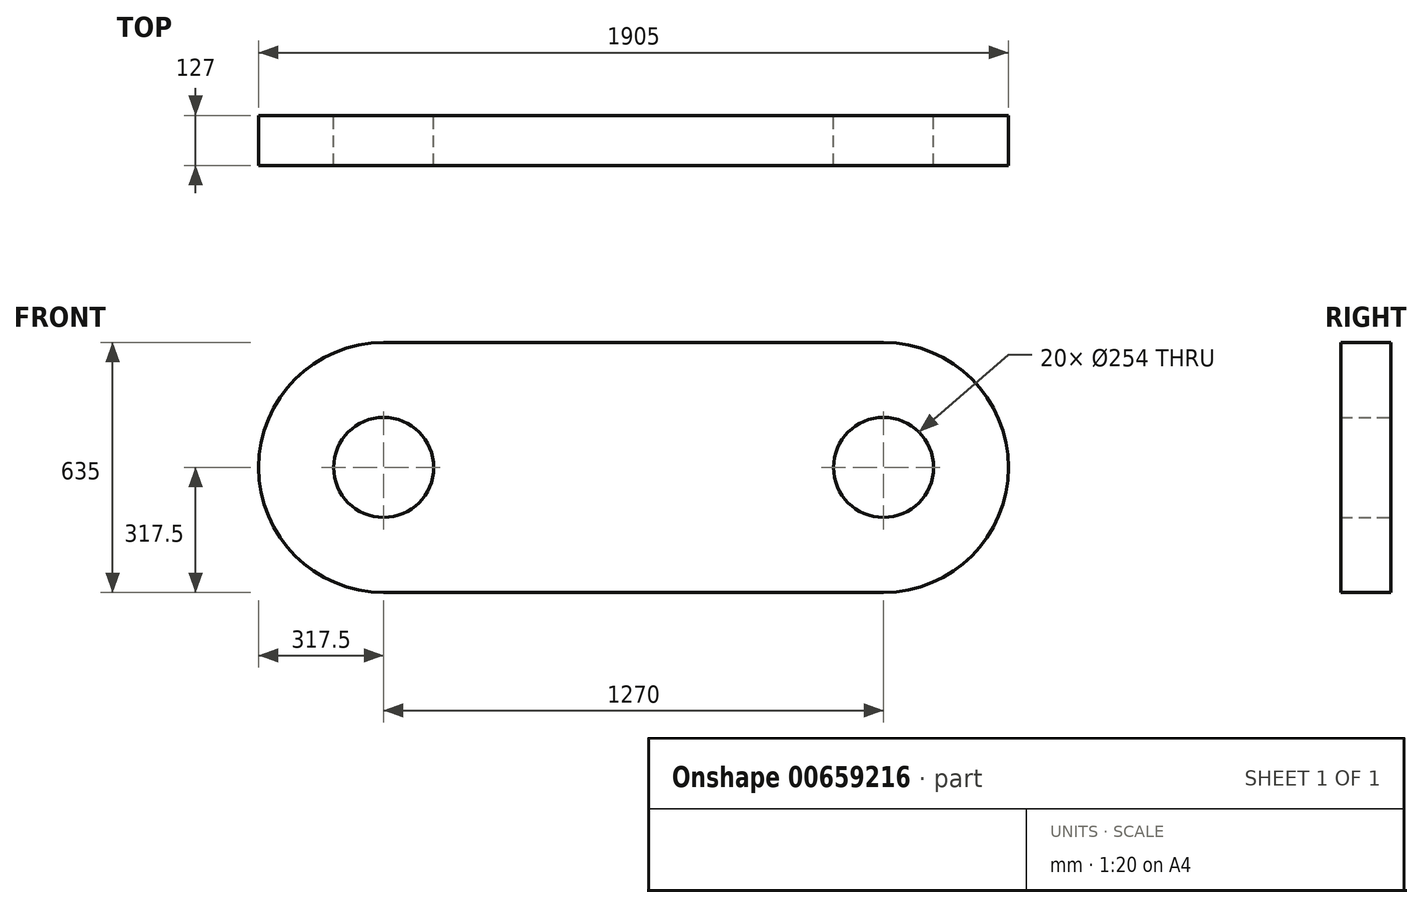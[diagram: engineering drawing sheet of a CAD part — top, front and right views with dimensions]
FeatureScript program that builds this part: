
annotation { "Feature Type Name" : "Feature", "Feature Type Description" : "" }
export const myFeature = defineFeature(function(context is Context, id is Id, definition is map)
    precondition{}
    {
        {
            var Q0;
            Q0=qCreatedBy(makeId("Front.planeOp"),FACE);
            var sketch = newSketch(context, id + "F0", { "sketchPlane" : qUnion([Q0])});
            skLineSegment(sketch, "E0.bottom", {"start": v(-635, 317.5) * mm, "end": v(635, 317.5) * mm});
            skLineSegment(sketch, "E0.top", {"start": v(-635, -317.5) * mm, "end": v(635, -317.5) * mm});
            skArc(sketch, "E1", {"start": v(635, -317.5) * mm, "mid": v(952.5, 0) * mm, "end": v(635, 317.5) * mm});
            skArc(sketch, "E2", {"start": v(-635, 317.5) * mm, "mid": v(-952.5, 0) * mm, "end": v(-635, -317.5) * mm});
            skCircle(sketch, "E3", {"center": v(-635, 0) * mm, "radius": 127 * mm});
            skCircle(sketch, "E4", {"center": v(635, 0) * mm, "radius": 127 * mm});
            skSolve(sketch);
        }
        {
            var Q0;
            Q0 = qSketchRegion(id + "F0", true);
            extrude(context, id + "F1", {"entities" : qUnion([Q0]), "endBound" : BoundingType.SYMMETRIC, "depth" : 127 * mm, "offsetDistance" : 25.4 * mm});
        }
    });
